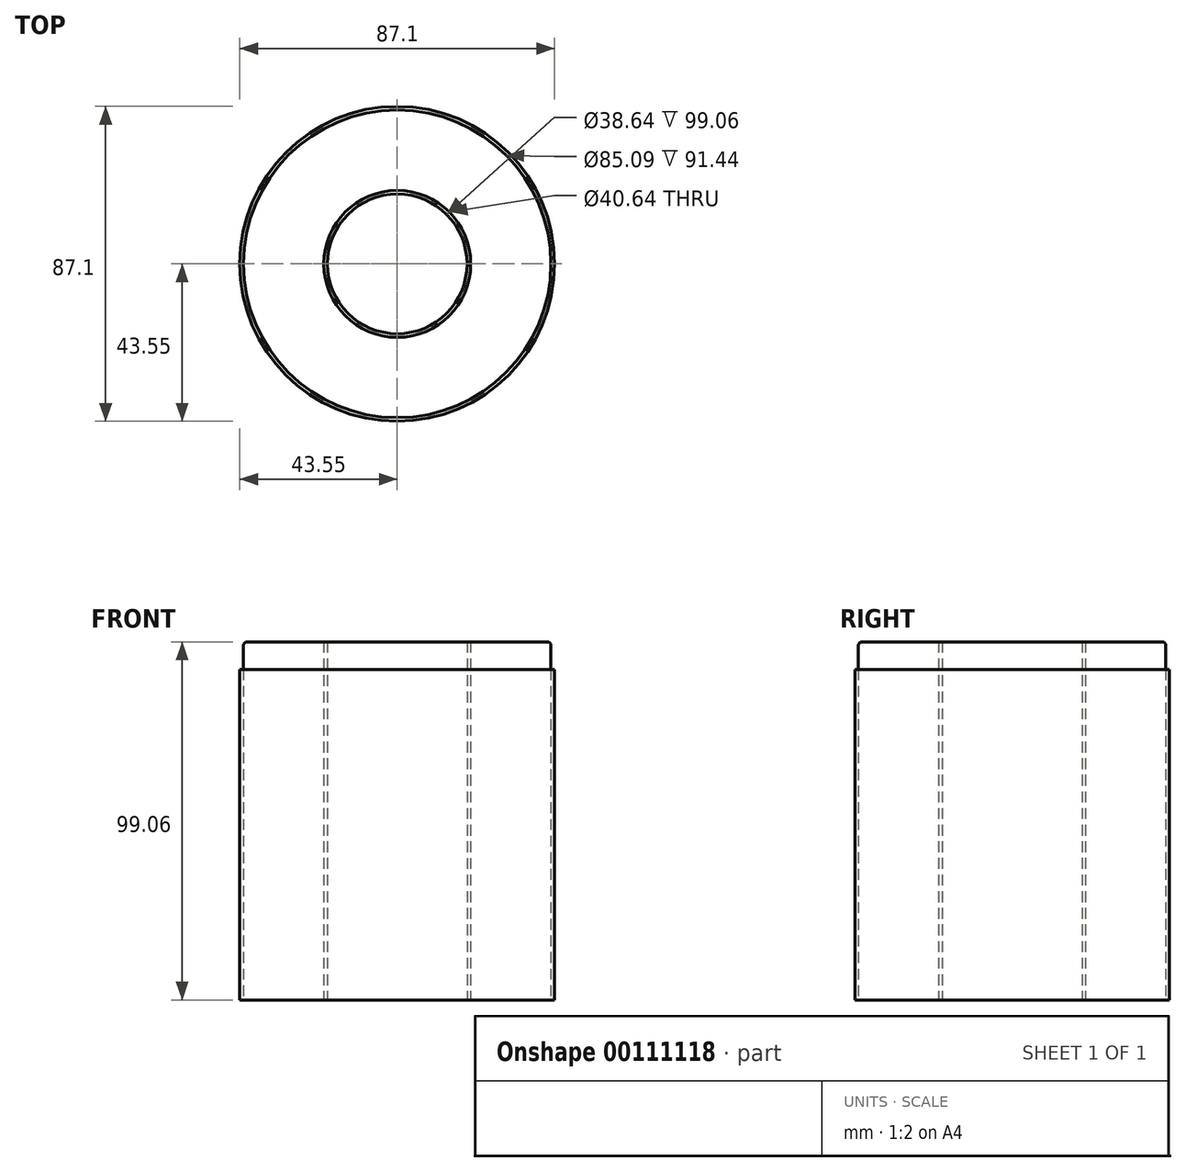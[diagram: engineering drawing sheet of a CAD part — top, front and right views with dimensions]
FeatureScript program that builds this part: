
annotation { "Feature Type Name" : "Feature", "Feature Type Description" : "" }
export const myFeature = defineFeature(function(context is Context, id is Id, definition is map)
    precondition{}
    {
        {
            var Q0;
            Q0=qCreatedBy(makeId("Top.planeOp"),FACE);
            var sketch = newSketch(context, id + "F0", { "sketchPlane" : qUnion([Q0])});
            skCircle(sketch, "E0", {"center": v(0, 0) * mm, "radius": 20.32 * mm});
            skCircle(sketch, "E1", {"center": v(0, 0) * mm, "radius": 42.55 * mm});
            skCircle(sketch, "E2.0", {"center": v(0, 0) * mm, "radius": 19.32 * mm});
            skCircle(sketch, "E3.0", {"center": v(0, 0) * mm, "radius": 43.55 * mm});
            skSolve(sketch);
        }
        {
            var Q0;
            Q0=makeQuery(id+"F0.imprint","IMPRINT",FACE,{"disambiguationData":[TD([[makeQuery(id+"F0.imprint","IMPRINT",EDGE,{"derivedFrom":sQuery(id+"F0.wireOp",EDGE,"E0")}),-1.0]])]});
            extrude(context, id + "F1", {"entities" : qUnion([Q0]), "depth" : 99.06 * mm});
        }
        {
            var Q0;
            Q0=makeQuery(id+"F1.opExtrude","CAP_EDGE",EDGE,{"disambiguationData":[OSD([sQuery(id+"F0.wireOp",EDGE,"E1")])],"isStart":false});
            fillet(context, id + "F2", {"entities" : qUnion([Q0]), "radius" : 1 * mm, "tangentPropagation" : true, "allowEdgeOverflow" : false});
        }
        {
            var Q0;
            Q0=makeQuery(id+"F0.imprint","IMPRINT",FACE,{"disambiguationData":[TD([[makeQuery(id+"F0.imprint","IMPRINT",EDGE,{"derivedFrom":sQuery(id+"F0.wireOp",EDGE,"E0")}),1.0]])]});
            extrude(context, id + "F3", {"entities" : qUnion([Q0]), "depth" : 99.06 * mm});
        }
        {
            var Q0;
            Q0=makeQuery(id+"F0.imprint","IMPRINT",FACE,{"disambiguationData":[TD([[makeQuery(id+"F0.imprint","IMPRINT",EDGE,{"derivedFrom":sQuery(id+"F0.wireOp",EDGE,"E1")}),-1.0]])]});
            extrude(context, id + "F4", {"entities" : qUnion([Q0]), "depth" : 91.44 * mm});
        }
    });
